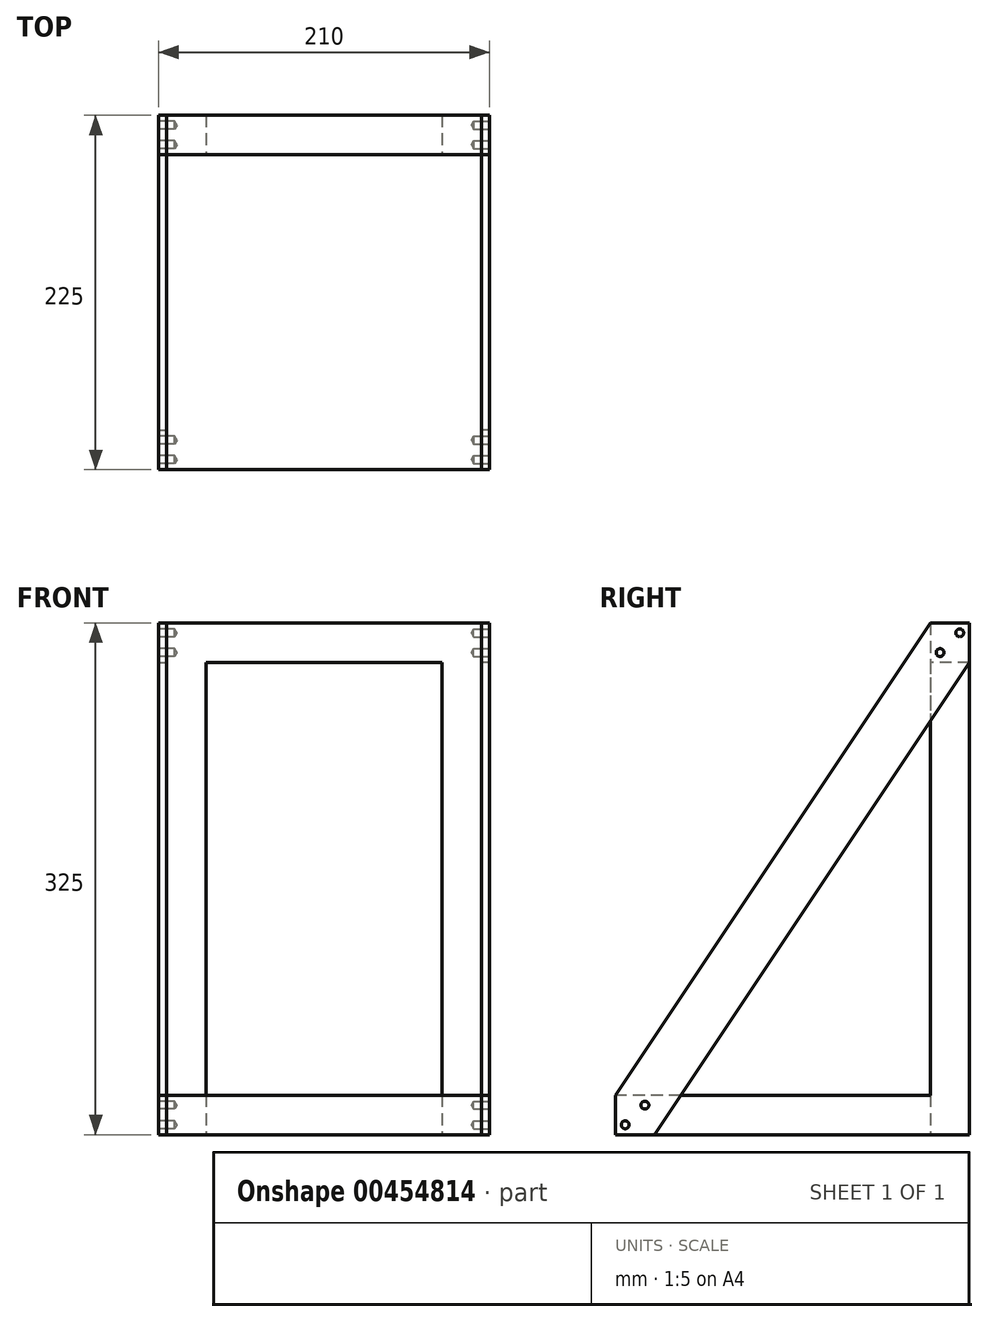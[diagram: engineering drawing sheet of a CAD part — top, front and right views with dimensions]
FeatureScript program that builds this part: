
annotation { "Feature Type Name" : "Feature", "Feature Type Description" : "" }
export const myFeature = defineFeature(function(context is Context, id is Id, definition is map)
    precondition{}
    {
        {
            var Q0;
            Q0=qCreatedBy(makeId("Top.planeOp"),FACE);
            var sketch = newSketch(context, id + "F0", { "sketchPlane" : qUnion([Q0])});
            skLineSegment(sketch, "E0.bottom", {"start": v(100, 100) * mm, "end": v(-100, 100) * mm});
            skLineSegment(sketch, "E0.top", {"start": v(100, -100) * mm, "end": v(-100, -100) * mm});
            skLineSegment(sketch, "E0.left", {"start": v(100, 100) * mm, "end": v(100, -100) * mm});
            skLineSegment(sketch, "E0.right", {"start": v(-100, 100) * mm, "end": v(-100, -100) * mm});
            skPoint(sketch, "E0.middle", {"position": v(0, 0) * mm});
            skSolve(sketch);
        }
        {
            var Q0;
            Q0 = qSketchRegion(id + "F0", true);
            extrude(context, id + "F1", {"entities" : qUnion([Q0]), "depth" : 25 * mm});
        }
        {
            var Q0;
            Q0=makeQuery(id+"F1.opExtrude","SWEPT_FACE",FACE,{"disambiguationData":[OSD([sQuery(id+"F0.wireOp",EDGE,"E0.bottom")])]});
            var sketch = newSketch(context, id + "F2", { "sketchPlane" : qUnion([Q0])});
            skLineSegment(sketch, "E1.bottom", {"start": v(-100, 25) * mm, "end": v(-75, 25) * mm});
            skLineSegment(sketch, "E1.top", {"start": v(-100, 0) * mm, "end": v(-75, 0) * mm});
            skLineSegment(sketch, "E1.left", {"start": v(-100, 25) * mm, "end": v(-100, 0) * mm});
            skLineSegment(sketch, "E1.right", {"start": v(-75, 25) * mm, "end": v(-75, 0) * mm});
            skLineSegment(sketch, "E2.bottom", {"start": v(100, 25) * mm, "end": v(75, 25) * mm});
            skLineSegment(sketch, "E2.top", {"start": v(100, 0) * mm, "end": v(75, 0) * mm});
            skLineSegment(sketch, "E2.left", {"start": v(100, 25) * mm, "end": v(100, 0) * mm});
            skLineSegment(sketch, "E2.right", {"start": v(75, 25) * mm, "end": v(75, 0) * mm});
            skSolve(sketch);
        }
        {
            var Q0;
            Q0 = qSketchRegion(id + "F2", true);
            extrude(context, id + "F3", {"entities" : qUnion([Q0]), "operationType" : NewBodyOperationType.ADD, "depth" : 25 * mm});
        }
        {
            var Q0;
            Q0=makeQuery(id+"F3.boolean.opBoolean","MERGE",FACE,{"derivedFrom":[makeQuery(id+"F1.opExtrude","CAP_FACE",FACE,{"disambiguationData":[OSD([sQuery(id+"F0.wireOp",EDGE,"E0.bottom"),sQuery(id+"F0.wireOp",EDGE,"E0.top"),sQuery(id+"F0.wireOp",EDGE,"E0.left"),sQuery(id+"F0.wireOp",EDGE,"E0.right")])],"isStart":false}),makeQuery(id+"F3.opExtrude","SWEPT_FACE",FACE,{"disambiguationData":[OSD([sQuery(id+"F2.wireOp",EDGE,"E1.bottom")])]}),makeQuery(id+"F3.opExtrude","SWEPT_FACE",FACE,{"disambiguationData":[OSD([sQuery(id+"F2.wireOp",EDGE,"E2.bottom")])]})]});
            var sketch = newSketch(context, id + "F4", { "sketchPlane" : qUnion([Q0])});
            skLineSegment(sketch, "E3.bottom", {"start": v(75, 100) * mm, "end": v(100, 100) * mm});
            skLineSegment(sketch, "E3.top", {"start": v(75, 125) * mm, "end": v(100, 125) * mm});
            skLineSegment(sketch, "E3.left", {"start": v(75, 100) * mm, "end": v(75, 125) * mm});
            skLineSegment(sketch, "E3.right", {"start": v(100, 100) * mm, "end": v(100, 125) * mm});
            skLineSegment(sketch, "E4.bottom", {"start": v(-75, 100) * mm, "end": v(-100, 100) * mm});
            skLineSegment(sketch, "E4.top", {"start": v(-75, 125) * mm, "end": v(-100, 125) * mm});
            skLineSegment(sketch, "E4.left", {"start": v(-75, 100) * mm, "end": v(-75, 125) * mm});
            skLineSegment(sketch, "E4.right", {"start": v(-100, 100) * mm, "end": v(-100, 125) * mm});
            skSolve(sketch);
        }
        {
            var Q0;
            Q0 = qSketchRegion(id + "F4", true);
            extrude(context, id + "F5", {"entities" : qUnion([Q0]), "operationType" : NewBodyOperationType.ADD, "depth" : 300 * mm});
        }
        {
            var Q0;
            Q0=makeQuery(id+"F5.boolean.opBoolean","MERGE",FACE,{"derivedFrom":[makeQuery(id+"F3.boolean.opBoolean","MERGE",FACE,{"derivedFrom":[makeQuery(id+"F1.opExtrude","SWEPT_FACE",FACE,{"disambiguationData":[OSD([sQuery(id+"F0.wireOp",EDGE,"E0.left")])]}),makeQuery(id+"F3.opExtrude","SWEPT_FACE",FACE,{"disambiguationData":[OSD([sQuery(id+"F2.wireOp",EDGE,"E1.left")])]})]}),makeQuery(id+"F5.opExtrude","SWEPT_FACE",FACE,{"disambiguationData":[OSD([sQuery(id+"F4.wireOp",EDGE,"E3.right")])]})]});
            var sketch = newSketch(context, id + "F6", { "sketchPlane" : qUnion([Q0])});
            skLineSegment(sketch, "E5", {"start": v(125, 325) * mm, "end": v(100, 325) * mm});
            skLineSegment(sketch, "E6", {"start": v(100, 325) * mm, "end": v(-100, 25) * mm});
            skLineSegment(sketch, "E7", {"start": v(-100, 25) * mm, "end": v(-100, 0) * mm});
            skLineSegment(sketch, "E8", {"start": v(125, 325) * mm, "end": v(125, 300) * mm});
            skLineSegment(sketch, "E9", {"start": v(-100, 0) * mm, "end": v(-75, 0) * mm});
            skLineSegment(sketch, "E10", {"start": v(-75, 0) * mm, "end": v(125, 300) * mm});
            skSolve(sketch);
        }
        {
            var Q0;
            Q0 = qSketchRegion(id + "F6", true);
            extrude(context, id + "F7", {"entities" : qUnion([Q0]), "depth" : 5 * mm});
        }
        {
            var Q0;
            Q0=makeQuery(id+"F7.opExtrude","CAP_FACE",FACE,{"disambiguationData":[OSD([sQuery(id+"F6.wireOp",EDGE,"E5"),sQuery(id+"F6.wireOp",EDGE,"E6"),sQuery(id+"F6.wireOp",EDGE,"E7"),sQuery(id+"F6.wireOp",EDGE,"E8"),sQuery(id+"F6.wireOp",EDGE,"E9"),sQuery(id+"F6.wireOp",EDGE,"E10")])],"isStart":false});
            var sketch = newSketch(context, id + "F8", { "sketchPlane" : qUnion([Q0])});
            skLineSegment(sketch, "E11.bottom", {"start": v(-100, 25) * mm, "end": v(-75, 25) * mm});
            skLineSegment(sketch, "E11.top", {"start": v(-100, 0) * mm, "end": v(-75, 0) * mm});
            skLineSegment(sketch, "E11.left", {"start": v(-100, 25) * mm, "end": v(-100, 0) * mm});
            skLineSegment(sketch, "E11.right", {"start": v(-75, 25) * mm, "end": v(-75, 0) * mm});
            skLineSegment(sketch, "E12.bottom", {"start": v(100, 325) * mm, "end": v(125, 325) * mm});
            skLineSegment(sketch, "E12.top", {"start": v(100, 300) * mm, "end": v(125, 300) * mm});
            skLineSegment(sketch, "E12.left", {"start": v(100, 325) * mm, "end": v(100, 300) * mm});
            skLineSegment(sketch, "E12.right", {"start": v(125, 325) * mm, "end": v(125, 300) * mm});
            skLineSegment(sketch, "E13", {"start": v(125, 325) * mm, "end": v(100, 300) * mm});
            skLineSegment(sketch, "E14", {"start": v(112.5, 312.5) * mm, "end": v(100, 300) * mm});
            skLineSegment(sketch, "E15", {"start": v(112.5, 312.5) * mm, "end": v(125, 325) * mm});
            skCircle(sketch, "E16", {"center": v(118.75, 318.75) * mm, "radius": 2.5 * mm});
            skCircle(sketch, "E17", {"center": v(106.25, 306.25) * mm, "radius": 2.5 * mm});
            skLineSegment(sketch, "E18", {"start": v(-75, 25) * mm, "end": v(-87.5, 12.5) * mm});
            skPoint(sketch, "E18.endSnap0", {"position": v(-87.5, 25) * mm});
            skPoint(sketch, "E18.endSnap1", {"position": v(-75, 12.5) * mm});
            skLineSegment(sketch, "E19", {"start": v(-87.5, 12.5) * mm, "end": v(-100, 0) * mm});
            skCircle(sketch, "E20", {"center": v(-93.75, 6.25) * mm, "radius": 2.5 * mm});
            skCircle(sketch, "E21", {"center": v(-81.25, 18.75) * mm, "radius": 2.5 * mm});
            skSolve(sketch);
        }
        {
            var Q0;
            Q0=sQuery(id+"F8.wireOp",VERTEX,"E21.center");
            var Q1;
            Q1=sQuery(id+"F8.wireOp",VERTEX,"E20.center");
            var Q2;
            Q2=sQuery(id+"F8.wireOp",VERTEX,"E16.center");
            var Q3;
            Q3=sQuery(id+"F8.wireOp",VERTEX,"E17.center");
            var Q4;
            Q4=makeQuery(id+"F1.opExtrude","SWEPT_BODY",BODY,{"disambiguationData":[OSD([sQuery(id+"F0.wireOp",EDGE,"E0.bottom"),sQuery(id+"F0.wireOp",EDGE,"E0.top"),sQuery(id+"F0.wireOp",EDGE,"E0.left"),sQuery(id+"F0.wireOp",EDGE,"E0.right")])]});
            var Q5;
            Q5=makeQuery(id+"F7.opExtrude","SWEPT_BODY",BODY,{"disambiguationData":[OSD([sQuery(id+"F6.wireOp",EDGE,"E5"),sQuery(id+"F6.wireOp",EDGE,"E6"),sQuery(id+"F6.wireOp",EDGE,"E7"),sQuery(id+"F6.wireOp",EDGE,"E8"),sQuery(id+"F6.wireOp",EDGE,"E9"),sQuery(id+"F6.wireOp",EDGE,"E10")])]});
            hole(context, id + "F9", {"style" : HoleStyle.SIMPLE, "endStyle" : HoleEndStyle.BLIND, "holeDiameter" : 5 * mm, "holeDepth" : 10 * mm, "isTappedThrough" : true, "tappedDepth" : 12 * mm, "tapClearance" : 3, "locations" : qUnion([Q0, Q1, Q2, Q3]), "scope" : qUnion([Q4, Q5])});
        }
        {
            var Q0;
            Q0=makeQuery(id+"F5.opExtrude","CAP_FACE",FACE,{"disambiguationData":[OSD([sQuery(id+"F4.wireOp",EDGE,"E4.bottom"),sQuery(id+"F4.wireOp",EDGE,"E4.top"),sQuery(id+"F4.wireOp",EDGE,"E4.left"),sQuery(id+"F4.wireOp",EDGE,"E4.right")])],"isStart":false});
            var sketch = newSketch(context, id + "F10", { "sketchPlane" : qUnion([Q0])});
            skLineSegment(sketch, "E22.bottom", {"start": v(-100, 125) * mm, "end": v(0, 125) * mm});
            skLineSegment(sketch, "E22.top", {"start": v(-100, -142.62) * mm, "end": v(0, -142.62) * mm});
            skLineSegment(sketch, "E22.left", {"start": v(-100, 125) * mm, "end": v(-100, -142.62) * mm});
            skLineSegment(sketch, "E22.right", {"start": v(0, 125) * mm, "end": v(0, -142.62) * mm});
            skSolve(sketch);
        }
        {
            var Q0;
            Q0 = qSketchRegion(id + "F10", true);
            extrude(context, id + "F11", {"entities" : qUnion([Q0]), "operationType" : NewBodyOperationType.REMOVE, "endBound" : BoundingType.THROUGH_ALL, "oppositeDirection" : true, "depth" : 25 * mm});
        }
        {
            var Q0;
            Q0=makeQuery(id+"F7.opExtrude","SWEPT_BODY",BODY,{"disambiguationData":[OSD([sQuery(id+"F6.wireOp",EDGE,"E5"),sQuery(id+"F6.wireOp",EDGE,"E6"),sQuery(id+"F6.wireOp",EDGE,"E7"),sQuery(id+"F6.wireOp",EDGE,"E8"),sQuery(id+"F6.wireOp",EDGE,"E9"),sQuery(id+"F6.wireOp",EDGE,"E10")])]});
            var Q1;
            Q1=makeQuery(id+"F1.opExtrude","SWEPT_BODY",BODY,{"disambiguationData":[OSD([sQuery(id+"F0.wireOp",EDGE,"E0.bottom"),sQuery(id+"F0.wireOp",EDGE,"E0.top"),sQuery(id+"F0.wireOp",EDGE,"E0.left"),sQuery(id+"F0.wireOp",EDGE,"E0.right")])]});
            var Q2;
            Q2=makeQuery(id+"F11.boolean.opBoolean","COPY",FACE,{"derivedFrom":makeQuery(id+"F11.opExtrude","SWEPT_FACE",FACE,{"disambiguationData":[OSD([sQuery(id+"F10.wireOp",EDGE,"E22.right")])]})});
            mirror(context, id + "F12", {"entities" : qUnion([Q0, Q1]), "mirrorPlane" : qUnion([Q2])});
        }
        {
            var Q0;
            Q0=makeQuery(id+"F12.opPattern","COPY",FACE,{"derivedFrom":makeQuery(id+"F5.boolean.opBoolean","MERGE",FACE,{"derivedFrom":[makeQuery(id+"F3.opExtrude","SWEPT_FACE",FACE,{"disambiguationData":[OSD([sQuery(id+"F2.wireOp",EDGE,"E1.right")])]}),makeQuery(id+"F5.opExtrude","SWEPT_FACE",FACE,{"disambiguationData":[OSD([sQuery(id+"F4.wireOp",EDGE,"E3.left")])]})]}),"instanceName":"1"});
            var sketch = newSketch(context, id + "F13", { "sketchPlane" : qUnion([Q0])});
            skLineSegment(sketch, "E23.bottom", {"start": v(100, 325) * mm, "end": v(125, 325) * mm});
            skLineSegment(sketch, "E23.top", {"start": v(100, 300) * mm, "end": v(125, 300) * mm});
            skLineSegment(sketch, "E23.left", {"start": v(100, 325) * mm, "end": v(100, 300) * mm});
            skLineSegment(sketch, "E23.right", {"start": v(125, 325) * mm, "end": v(125, 300) * mm});
            skSolve(sketch);
        }
        {
            var Q0;
            Q0 = qSketchRegion(id + "F13", true);
            var Q1;
            Q1=makeQuery(id+"F5.boolean.opBoolean","MERGE",FACE,{"derivedFrom":[makeQuery(id+"F3.opExtrude","SWEPT_FACE",FACE,{"disambiguationData":[OSD([sQuery(id+"F2.wireOp",EDGE,"E1.right")])]}),makeQuery(id+"F5.opExtrude","SWEPT_FACE",FACE,{"disambiguationData":[OSD([sQuery(id+"F4.wireOp",EDGE,"E3.left")])]})]});
            extrude(context, id + "F14", {"entities" : qUnion([Q0]), "operationType" : NewBodyOperationType.ADD, "endBound" : BoundingType.UP_TO_SURFACE, "endBoundEntityFace" : qUnion([Q1]), "depth" : 25 * mm});
        }
    });
